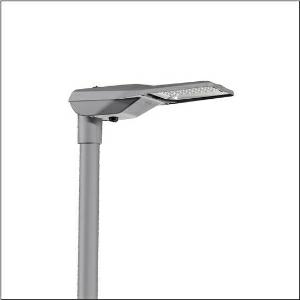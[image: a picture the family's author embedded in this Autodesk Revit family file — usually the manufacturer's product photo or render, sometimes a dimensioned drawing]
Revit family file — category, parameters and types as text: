
# Revit family: streetlight_sl_21_mini___pl52_5xe2h43t08hb_6adb
name_source: partatom
category: Lighting Fixtures
units: mm (PartAtom-declared; Revit-internal decimal feet)

## family parameters
Cut with Voids When Loaded = No
Host = Face
Light Source = No
Part Type = Normal
Room Calculation Point = No
Round Connector Dimension = Use Diameter
Shared = No

## types (1)
- --- (1 x LED, 9260 lm, 66 W, 4000K)
    Apparent Load = 66 VA
    CIE Flux Codes = 27 59 98 100 100
    Color Rendering = 70
    Color Temperature = 4000K
    Default Elevation = 1800 mm
    Description = Streetlight SL 21 mini, mast luminaire, primary light control with lens, of PMMA, primary optical cover: cover, of toughened safety glass, transparent, light distribution: PL52, light emission: direct distribution, primary light characteristic: asymmetric, installation type: side-entry, post-top, LED, High Power LED, rated luminous flux: 9.260lm, luminous efficacy: 140lm/W, light colour: 740, colour temperature: 4000K, control gear: D4i, control: overheat protection, constant luminous flux control, time-dependent luminous flux control, flexible luminous flux parameterisation, pre-setting: logarithmic dimming characteristic, mains connection: 220..240V, AC, 50/60Hz, start of lifetime: 66W, end of service life: 69W, reduction: 30W, luminaire housing, of diecast aluminium, powder-coated, Siteco® metallic grey (DB 702S), corrosivity category C5 mid according to DIN EN ISO 12944, please order mast flange separately, inclination adjustable: 0°, 5°, 10°, 15°, sealing non-destructively replaceable, multi-level sealing system, length: 628mm, width: 235mm, height: 110mm, mast flange for spigot size: 42mm (side-entry): 5XC10008XM4, 60/48mm (side-entry/post-top): 5XC10108XM2, 76/60mm (side-entry/post-top): 5XC10108XM1, mounting height: 4..8m, Smart Interface below and above, protection rating (complete): IP66, insulation class (complete): insulation class II (safety insulation), certification: CE, ENEC, ENEC+, VDE, impact resistance: IK10, permissible operating ambient temperature for outdoor applications: -40..+50°C, standard-compliant lighting for roads and squares, packaging unit: 1 piece

Light Distribution: PL52
    Height = 110 mm
    Lamp = 1 x LED
    Lamp Light Flux = 9260 lm
    Lamp Power = 66 W
    Lamp count = 1
    Length = 625 mm
    Luminous efficacy = 140 lm/W
    Manufacturer = Siteco
    ModVariant = No
    Model = 5XE2H43T08HB
    Number of Poles = 1
    OnlyDefault = Yes
    Power Factor = 1
    Product Name = Streetlight SL 21 mini | PL52
    Product group = mast luminaire | pylon top
    ProductGroupID = 6100
    Protection Class = Protection class II
    Protection Degree = IP 66
    RLX_Detail_Level = 1
    RLX_Emergency_Light_Flux = 0 lm
    RLX_Emergency_Type = 0
    RLX_Emergency_Type_DB = No
    RlxData = <blob elided: 35893 chars, md5=ade8bc46>
    Socket = socket
    Standby Power = 0 W
    System Light Flux = 9260 lm
    System Power = 66 W
    Type Comments = factory setting: luminous flux: 100 % | dim-lin: 254 | 670 mA
    Type Image = l_1003514.jpg
    URL = http://relux.com
    VarID = @adj_211247
    Voltage = 0 V
    Weight = 0.00 kg
    Width = 234 mm

## geometry (parser evidence)
native form markers: Blend x4, Sweep x11
no freeform markers — native parametric forms only
